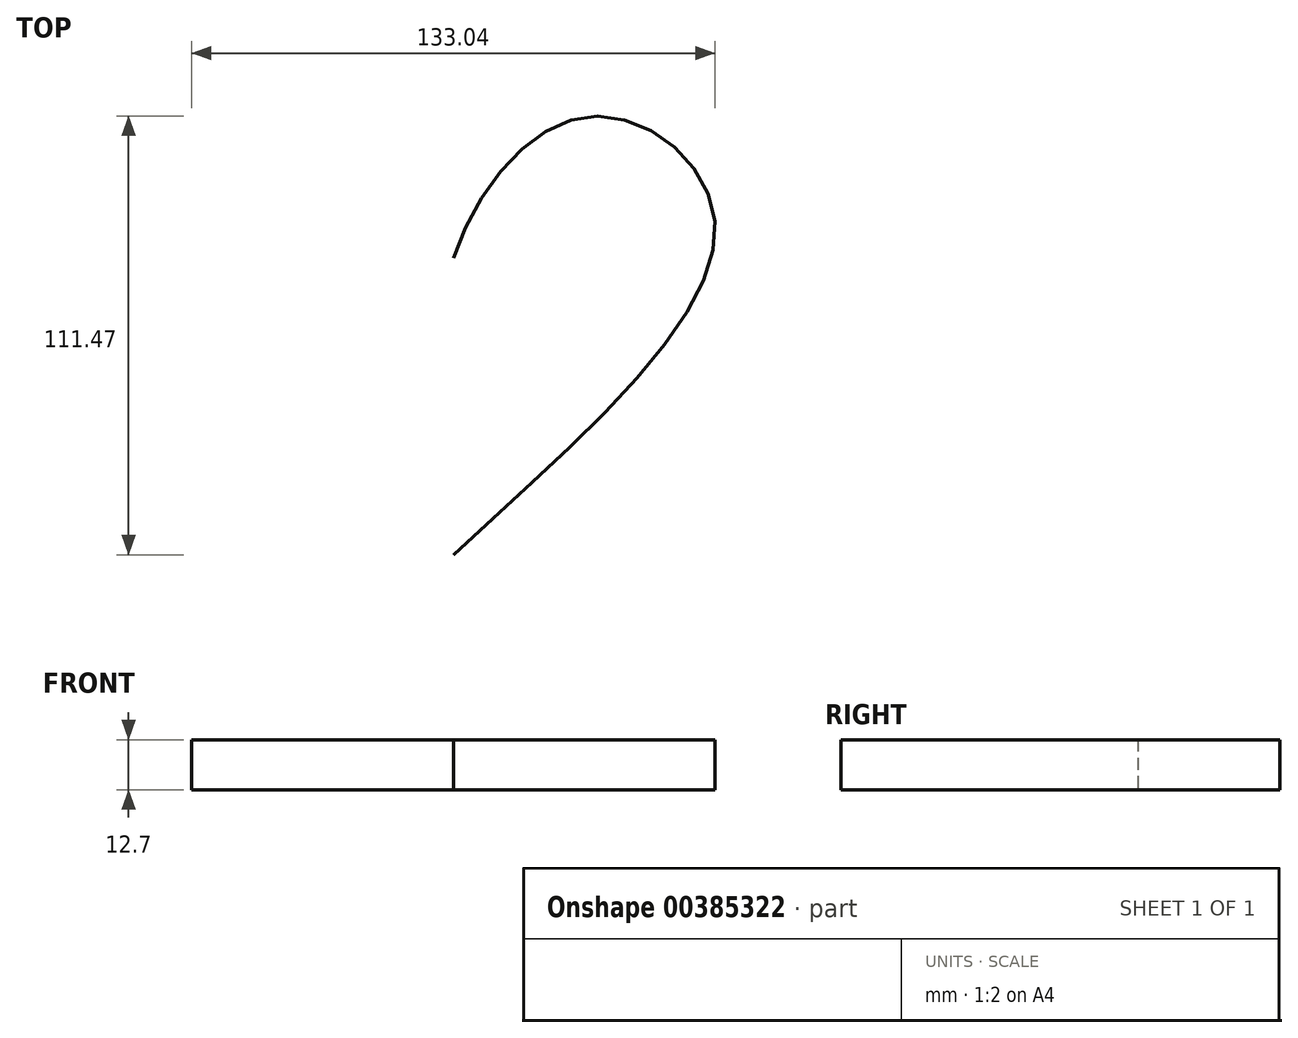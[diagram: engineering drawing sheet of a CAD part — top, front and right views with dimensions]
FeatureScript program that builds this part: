
annotation { "Feature Type Name" : "Feature", "Feature Type Description" : "" }
export const myFeature = defineFeature(function(context is Context, id is Id, definition is map)
    precondition{}
    {
        {
            var Q0;
            Q0=qCreatedBy(makeId("Top.planeOp"),FACE);
            var sketch = newSketch(context, id + "F0", { "sketchPlane" : qUnion([Q0])});
            skFitSpline(sketch, "E0", {"points": [v(0, 0) * mm, v(35.67, 36.11) * mm, v(66.43, 9.36) * mm, v(0, -75.34) * mm], "startDerivative": vector(60.28, 183.17) * mm, "endDerivative": vector(-231.82, -212.68) * mm});
            skFitSpline(sketch, "E1.MirrorCS", {"points": [v(0, 0) * mm, v(-35.67, 36.11) * mm, v(-66.43, 9.36) * mm, v(0, -75.34) * mm], "startDerivative": vector(-60.28, 183.17) * mm, "endDerivative": vector(231.82, -212.68) * mm});
            skSolve(sketch);
        }
        {
            var Q0;
            Q0 = qSketchRegion(id + "F0", true);
            extrude(context, id + "F1", {"entities" : qUnion([Q0]), "depth" : 12.7 * mm, "offsetDistance" : 25.4 * mm});
        }
    });
